# Revit family: R-MTI-111
name_source: partatom
category: Portes
units: mm (PartAtom-declared; Revit-internal decimal feet)

## family parameters
Couper avec des vides une fois chargée = Non
Hôte = Mur
Partagée = Non
Repère de localisation dans la pièce = Oui
Toujours verticalement = Non

## types (1)
- MTI-111
    ----- PARAMETRES DE L'HÔTE -------------------- = .
    ----- PARAMETRES DES VANTAUX -------------------- = .
    ----- PARAMETRES POSITION HUISSERIE -------------------- = .
    ----- PARAMETRES PROFIL -------------------- = .
    ----- TYPE D'HUISSERIE -------------------- = .
    ----- TYPE DE VANTAIL -------------------- = .
    --------- EQUIPEMENTS ----------------- = .
    1 Vantail = Oui
    2 Vantaux = Non
    A.E.V = A*3.E*3B.V*C2
    Acoustique = Rw (C ; Ctr) = 36(-1 ; -3)
    Code_MAJ = 2304120802MTI111
    Coloris Oculus = Peinture Laquée PMT - Bleu Gris - RAL 5008
    Coloris Oculus Métal = Peinture Laquée PMT - Bleu Gris - RAL 5008
    Coloris protection parement PVC = Acrylique
    Coloris_Chants = Peinture Laquée PMT - Bleu Gris - RAL 5008
    Construction analytique = <Aucun>
    DAS = Non
    Description = Bloc-porte métal issues de secours et de service M101LSA36 1 vantail, simple action, 36(-1; -3) dB, 1,5 W/m².K, A*3.E*3B.V*C2, sur huisserie métal
    Décalage_Largeur_Profil = 0 mm  [stored 0 ft]
    Décalage_Profondeur_Profil = 0 mm  [stored 0 ft]
    Décalage_Seuil_Vantail = 0 mm  [stored 0 ft]
    Désaffleurement_Vantail = 0 mm  [stored 0 ft]
    Ep_Tôle_Profil = 2 mm  [stored 0.00656168 ft]
    Epaisseurs_Vantaux = 57 mm  [stored 0.187008 ft]
    Espacement_Paumelle_Vantail = 10 mm  [stored 0.0328084 ft]
    Fabricant = MALERBA
    Ferrage_Encastre = Non
    Feuillure_Basse_Vantail = Non
    Fiche_Produit = MTI-111
    Hauteur Feuillure Basse Vantail = 15 mm  [stored 0.0492126 ft]
    Hauteur protection parement PVC = 600 mm  [stored 1.9685 ft]
    Hauteur_Axe_Bequille = 1045 mm  [stored 3.42848 ft]
    Hauteur_Vantaux_Souhaitée = 2114 mm  [stored 6.9357 ft]
    Ht Microviseur = 1500 mm  [stored 4.92126 ft]
    Huisserie_Bati_d'Angle = Non
    Huisserie_HB_Banches = Non
    Huisserie_HT_RV_Avec_contre_Feuillure = Non
    Huisserie_HT_RV_Sans_contre_Feuillure = Oui
    Huisserie_Reprise_de_Doublage = Non
    Inv_Espacement_Paumelle_Vantail = 10 mm  [stored 0.0328084 ft]
    Inv_Position_Largeur_Paumelle = 10 mm  [stored 0.0328084 ft]
    Jeu Profondeur Recouvrement Vantail = 0 mm  [stored 0 ft]
    Jeu_1 = 5 mm  [stored 0.0164042 ft]
    Jeu_2 = 5 mm  [stored 0.0164042 ft]
    Jeu_Côté_Articulation_Vantail = 4 mm  [stored 0.0131234 ft]
    Jeu_Côté_Fermeture_Vantail = 4 mm  [stored 0.0131234 ft]
    Jeu_Haut = 5 mm  [stored 0.0164042 ft]
    Jeu_Traverse_Basse_Vantail = 8 mm  [stored 0.0262467 ft]
    Jeu_Traverse_Haute_Vantail = 3 mm  [stored 0.00984252 ft]
    Largeur Feuillure Battement Articulation = 15 mm  [stored 0.0492126 ft]
    Largeur_Axe_Bequille = 60 mm  [stored 0.19685 ft]
    Largeur_Contre_Feuillure_Profil = 25 mm  [stored 0.082021 ft]
    Largeur_Feuillure_Battement_Semi_Fixe = 15 mm  [stored 0.0492126 ft]
    Largeur_Feuillure_Battement_Service = 15 mm  [stored 0.0492126 ft]
    Largeur_Feuillure_Profil = 25 mm  [stored 0.082021 ft]
    Largeur_Feuillure_hôte_coté_opposé = 0 mm  [stored 0 ft]
    Largeur_Feuillure_hôte_coté_ouvrant = 0 mm  [stored 0 ft]
    Largeur_Parement_coté_Feuillure_Profil = 30 mm  [stored 0.0984252 ft]
    Largeur_Parement_coté_opposé_Feuillure_Profil = 55 mm  [stored 0.180446 ft]
    Largeur_Vantail_Semi_Fixe_Souhaitée = 925 mm  [stored 3.03478 ft]
    Largeur_Vantail_Service_Souhaitée = 942 mm  [stored 3.09055 ft]
    Materiau_Scellement = <Par catégorie>
    Materiaux_Dominant = Métal
    Maternelle = Non
    Microviseur = Non
    Modèle = 53-SA-HM
    Nombre_Vantaux = 1
    Note d'identification = 1V - ACOUSTIQUE 36 / AEV / THERMIQUE - BATTANTE NON FEU
    Paumelle 5 inversée = Non
    Paumelle_1 = 230 mm  [stored 0.754593 ft]
    Paumelle_2 = 859 mm  [stored 2.81824 ft]
    Paumelle_3 = 859 mm  [stored 2.81824 ft]
    Paumelle_4 = 165 mm
    Paumelle_5 inversée = 165 mm
    Position_Largeur_Paumelle = 4 mm  [stored 0.0131234 ft]
    Profondeur Feuillure Basse Vantail = 25 mm  [stored 0.082021 ft]
    Profondeur Feuillure Battement Articulation = 26 mm
    Profondeur_Contre_Feuillure_Profil = 30 mm  [stored 0.0984252 ft]
    Profondeur_Feuillure_Battement_Semi_Fixe = 14 mm  [stored 0.0459318 ft]
    Profondeur_Feuillure_Battement_Service = 26 mm
    Profondeur_Feuillure_Profil = 62 mm  [stored 0.203412 ft]
    Profondeur_Feuillure_hôte_coté_opposé = 0 mm  [stored 0 ft]
    Profondeur_Feuillure_hôte_coté_ouvrant = 0 mm  [stored 0 ft]
    Profondeur_Retour_Parement_Profil = 12 mm  [stored 0.0393701 ft]
    Profondeur_Totale_Pose_Tunnel_Profil = 115 mm  [stored 0.377297 ft]
    Protection de parement PVC coté opposé aux paumelles = Non
    Protection de parement pvc côté paumelles = Non
    Reference_Commerciale = M101LSA36
    Reprise_Doublage_1 = 0 mm  [stored 0 ft]
    Reprise_Doublage_2 = 0 mm  [stored 0 ft]
    Reprise_Doublage_Haut = 0 mm  [stored 0 ft]
    Thermique (W/m2.°K) = 1.5
    URL = https://www.malerba.fr
    Visibilite_Paum-4 = Oui
    Visibilite_Poignee = Oui

note: [stored X ft] marks values corroborated as IEEE doubles in the binary element streams (Revit-internal decimal feet)

## geometry (parser evidence)
native form markers: Blend x28
no freeform markers — native parametric forms only
